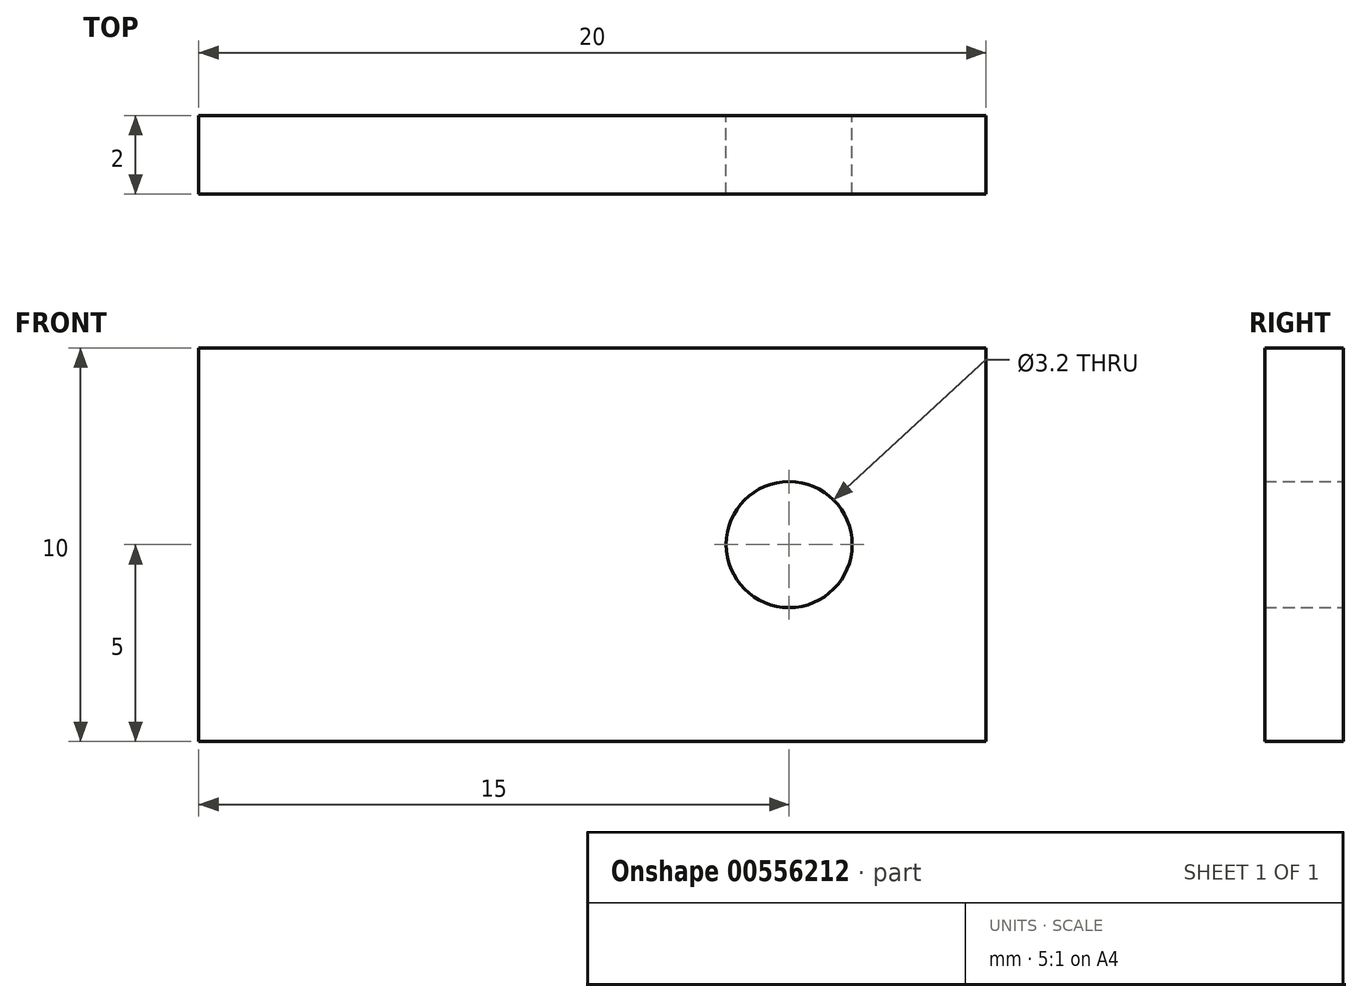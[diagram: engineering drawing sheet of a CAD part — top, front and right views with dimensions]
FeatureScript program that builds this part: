
annotation { "Feature Type Name" : "Feature", "Feature Type Description" : "" }
export const myFeature = defineFeature(function(context is Context, id is Id, definition is map)
    precondition{}
    {
        {
            var Q0;
            Q0=qCreatedBy(makeId("Front.planeOp"),FACE);
            var sketch = newSketch(context, id + "F0", { "sketchPlane" : qUnion([Q0])});
            skLineSegment(sketch, "E0.bottom", {"start": v(0, 0) * mm, "end": v(20, 0) * mm});
            skLineSegment(sketch, "E0.top", {"start": v(0, 10) * mm, "end": v(20, 10) * mm});
            skLineSegment(sketch, "E0.left", {"start": v(0, 0) * mm, "end": v(0, 10) * mm});
            skLineSegment(sketch, "E0.right", {"start": v(20, 0) * mm, "end": v(20, 10) * mm});
            skCircle(sketch, "E1", {"center": v(15, 5) * mm, "radius": 1.6 * mm});
            skSolve(sketch);
        }
        {
            var Q0;
            Q0 = qSketchRegion(id + "F0", true);
            extrude(context, id + "F1", {"entities" : qUnion([Q0]), "depth" : 2 * mm, "offsetDistance" : 25 * mm});
        }
    });
